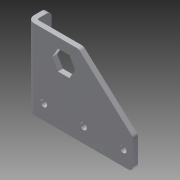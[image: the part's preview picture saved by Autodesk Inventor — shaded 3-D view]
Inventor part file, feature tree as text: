
AUTODESK INVENTOR PART (.ipt)
format: ipt  version: 2014 (Build 180170000, 170)  size: 130,048 bytes
history: native  units: in
note: dims shown in document units (in); Inventor stores cm internally (conversion verified against a paired STEP export)
features: sheet_metal_op x4, sketch x2, other x2, fillet x1
ambient origin geometry x8: Origin, YZ Plane, XZ Plane, XY Plane, X Axis, Y Axis, Z Axis, Center Point
bodies: Solid1 (feature_tree)
feature tree (9):
  sheet_metal_op  "Face1"
  sheet_metal_op  "Flange2"
  fillet  "Fillet1"  Radius=0.125in
  sketch  "Sketch1"  dims[d5=2.5in d6=0.163in d7=0.25in d8=0.375in d11=0.125in]
  other  "Plate1"
  sketch  "Sketch3"  dims[d22=1.1811in d24=1.0in d25=0.3937in d27=1.0in d29=2.0in d30=0.75in d31=1.125in d32=0.5in d34=0.75in d35=0.5in d36=0.125in d37=0.0625in d38=0.25in d39=0.125in d40=0.5in d41=90.0deg d42=0.05in d43=0.5in d44=0.125in d45=0.125in d46=0.125in]
  other  "Plate3"
  sheet_metal_op  "Bend2"
  sheet_metal_op  "Corner2"
